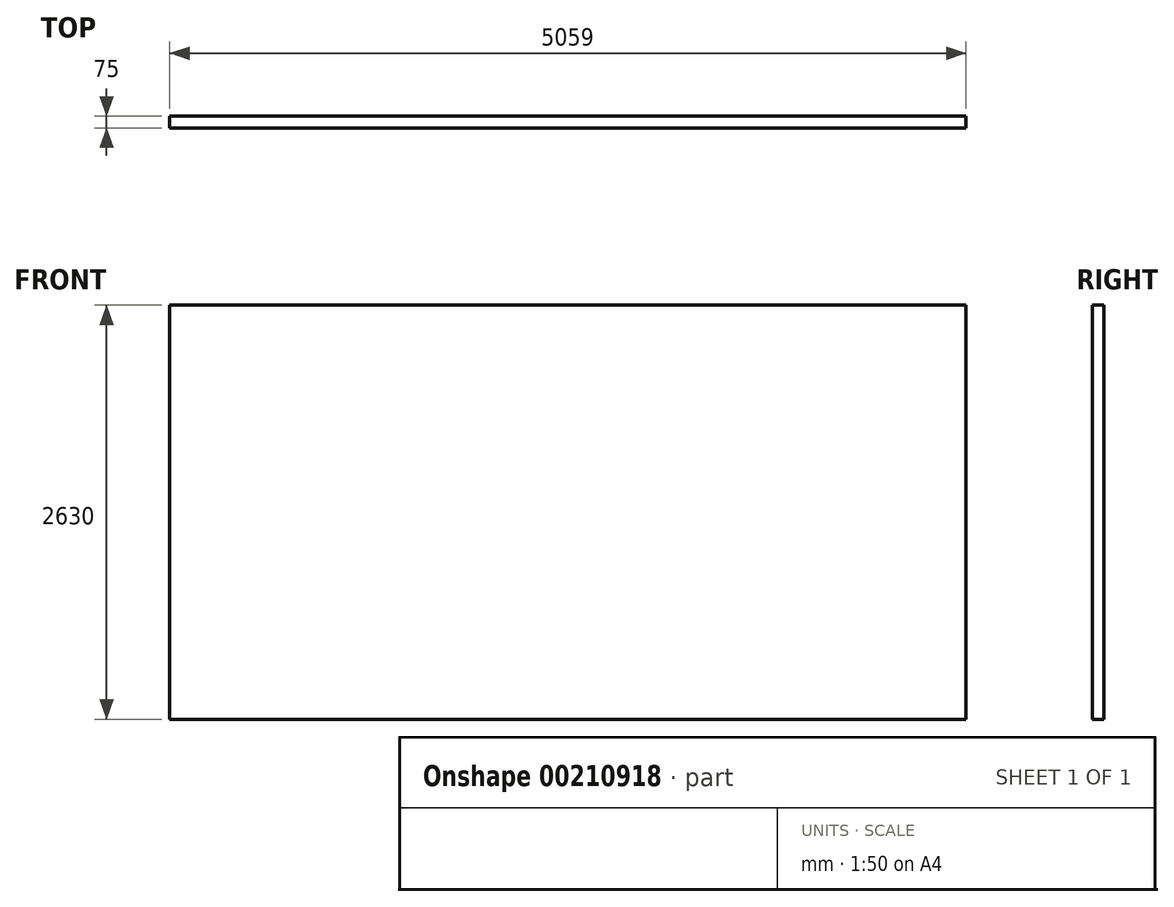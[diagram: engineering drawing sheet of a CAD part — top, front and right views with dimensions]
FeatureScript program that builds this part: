
annotation { "Feature Type Name" : "Feature", "Feature Type Description" : "" }
export const myFeature = defineFeature(function(context is Context, id is Id, definition is map)
    precondition{}
    {
        {
            var Q0;
            Q0=qCreatedBy(makeId("Front.planeOp"),FACE);
            var sketch = newSketch(context, id + "F0", { "sketchPlane" : qUnion([Q0])});
            skLineSegment(sketch, "E0.bottom", {"start": v(0, 0) * mm, "end": v(5059, 0) * mm});
            skLineSegment(sketch, "E0.right", {"start": v(5059, 0) * mm, "end": v(5059, 2630) * mm});
            skLineSegment(sketch, "E1", {"start": v(0, 2630) * mm, "end": v(5059, 2630) * mm});
            skLineSegment(sketch, "E2", {"start": v(0, 0) * mm, "end": v(0, 2630) * mm});
            skSolve(sketch);
        }
        {
            var Q0;
            Q0=makeQuery(id+"F0.imprint","IMPRINT",FACE,{"disambiguationData":[TD([[makeQuery(id+"F0.imprint","IMPRINT",EDGE,{"derivedFrom":sQuery(id+"F0.wireOp",EDGE,"E0.bottom")}),1.0]])]});
            extrude(context, id + "F1", {"entities" : qUnion([Q0]), "depth" : 75 * mm});
        }
    });
